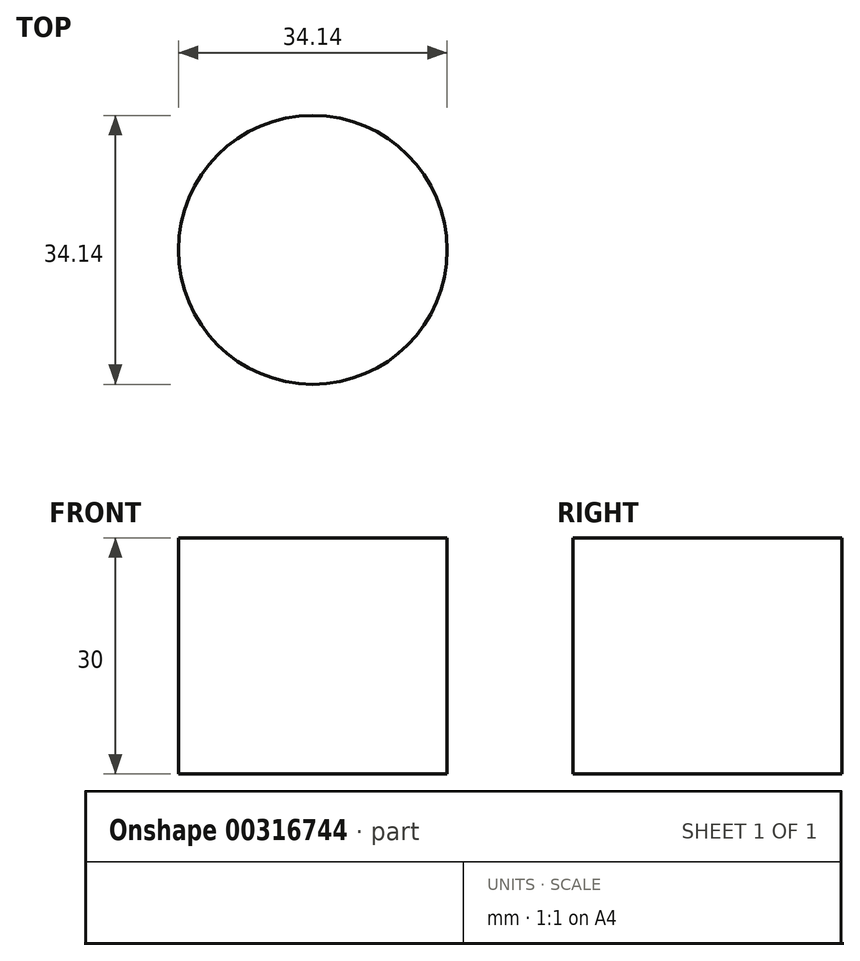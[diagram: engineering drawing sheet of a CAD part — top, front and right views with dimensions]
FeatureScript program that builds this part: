
annotation { "Feature Type Name" : "Feature", "Feature Type Description" : "" }
export const myFeature = defineFeature(function(context is Context, id is Id, definition is map)
    precondition{}
    {
        {
            var Q0;
            Q0=qCreatedBy(makeId("Top.planeOp"),FACE);
            var sketch = newSketch(context, id + "F0", { "sketchPlane" : qUnion([Q0])});
            skCircle(sketch, "E0", {"center": v(0, 0) * mm, "radius": 17.07 * mm});
            skSolve(sketch);
        }
        {
            var Q0;
            Q0=makeQuery(id+"F0.imprint","IMPRINT",FACE,{"disambiguationData":[TD([[makeQuery(id+"F0.imprint","IMPRINT",EDGE,{"derivedFrom":sQuery(id+"F0.wireOp",EDGE,"E0")}),1.0]])]});
            extrude(context, id + "F1", {"entities" : qUnion([Q0]), "depth" : 30 * mm});
        }
        {
            var Q0;
            Q0=makeQuery(id+"F1.opExtrude","CAP_FACE",FACE,{"disambiguationData":[OSD([sQuery(id+"F0.wireOp",EDGE,"E0")])],"isStart":false});
            cPlane(context, id + "F2", {"entities" : qUnion([Q0]), "cplaneType" : CPlaneType.OFFSET, "offset" : 0 * mm, "width" : 150 * mm, "height" : 150 * mm});
        }
    });
